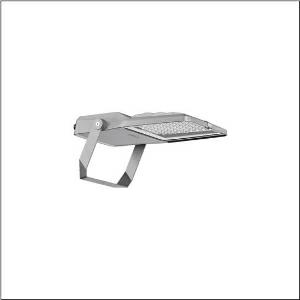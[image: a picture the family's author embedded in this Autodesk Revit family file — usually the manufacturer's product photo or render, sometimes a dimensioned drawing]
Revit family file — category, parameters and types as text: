
# Revit family: floodlight_fl_21_mini___pl52_5xa7772c4d1a_ce37
name_source: partatom
category: Lighting Fixtures
units: mm (PartAtom-declared; Revit-internal decimal feet)

## family parameters
Cut with Voids When Loaded = No
Host = Face
Light Source = No
Part Type = Normal
Room Calculation Point = No
Round Connector Dimension = Use Diameter
Shared = No

## types (1)
- --- (1 x LED, 12720 lm, 87.2 W, 4000K)
    Apparent Load = 87 VA
    CIE Flux Codes = 26 60 98 100 100
    Color Rendering = 70
    Color Temperature = 4000K
    Default Elevation = 1800 mm
    Description = Floodlight FL 21 mini, floodlight, primary light control with lens, of PMMA, primary optical cover: protective disc, of toughened safety glass, transparent, light distribution: PL52, light emission: direct distribution, installation type: surface-mounted, LED, High Power LED, rated luminous flux: 12.720lm, luminous efficacy: 146lm/W, light colour: 740, colour temperature: 4000K, control gear: ECG iQ, control: Street-Remote, Auto-Match, Temp-Guard, Night-Set, Smart-Wire, Desk-Remote (wireless, voltage-free reading and setting of iQ features in the workshop via application-optimized NFC function/RFID function), optimised constant luminous flux control (CLO 2.0), with terminal, 6-pole, mains connection: 220..240V, AC, 50/60Hz, start of lifetime: 87W, end of lifetime: 92W, reduction: 40W, luminaire housing, of diecast aluminium, powder-coated, Siteco® metallic grey (DB 702S), corrosivity category C5 according to DIN EN ISO 12944, mounting bracket, of steel, galvanised, powder-coated, Siteco® metallic grey (DB 702S), protection rating (complete): IP66, insulation class (complete): insulation class II (safety insulation), certification: CE, ENEC, VDE, protection symbol: D, impact resistance: IK08, permissible operating ambient temperature: -40..+40°C, permissible operating ambient temperature for outdoor applications: -40..+50°C, standard: DIN EN 12944, packaging unit: 1 piece

Light Distribution: PL52
    Height = 70 mm
    Lamp = 1 x LED
    Lamp Light Flux = 12720 lm
    Lamp Power = 87.2 W
    Lamp count = 1
    Length = 485 mm
    Luminous efficacy = 146 lm/W
    Manufacturer = Siteco
    ModVariant = No
    Model = 5XA7772C4D1A
    Number of Poles = 1
    OnlyDefault = Yes
    Power Factor = 1
    Product Name = Floodlight FL 21 mini | PL52
    Product group = floodlight | pylon top
    ProductGroupID = 6101
    Protection Class = Protection class II
    Protection Degree = IP 66
    RLX_Detail_Level = 1
    RlxData = <blob elided: 96217 chars, md5=7f193182>
    Socket = socket
    Standby Power = 0 W
    System Light Flux = 12720 lm
    System Power = 87 W
    Type Comments = factory setting: luminous flux: 100 % | dim-lin: 254 | 456 mA
    Type Image = l_1006845.jpg
    URL = http://relux.com
    VarID = @adj_075351
    Voltage = 0 V
    Weight = 0.00 kg
    Width = 337 mm

## geometry (parser evidence)
native form markers: Blend x4, Sweep x11
no freeform markers — native parametric forms only
